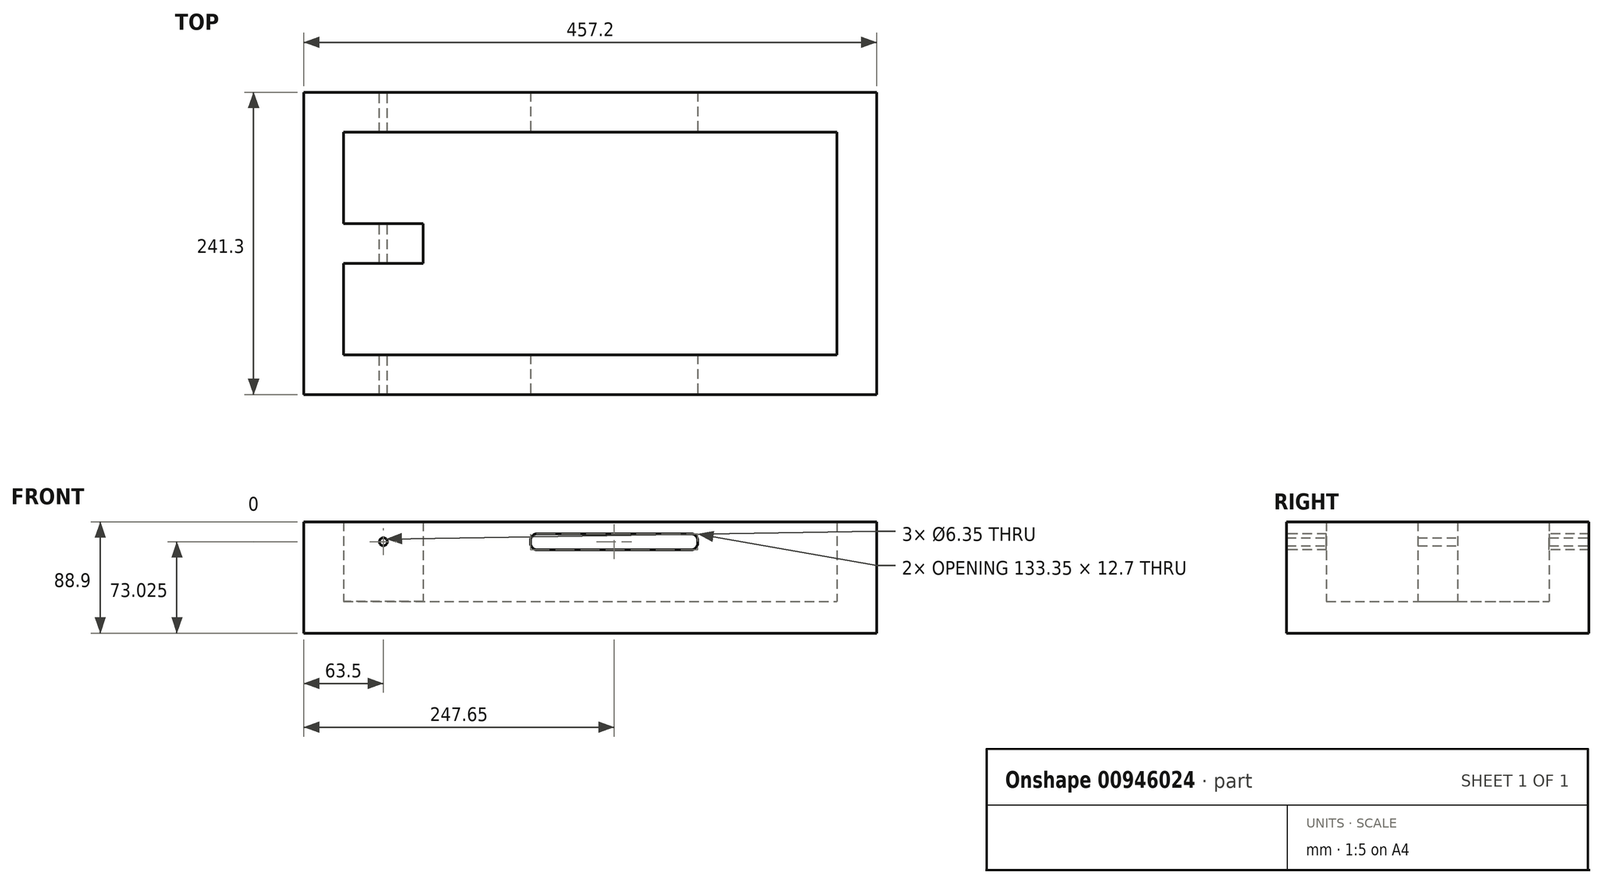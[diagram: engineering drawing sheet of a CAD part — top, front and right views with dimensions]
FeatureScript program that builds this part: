
annotation { "Feature Type Name" : "Feature", "Feature Type Description" : "" }
export const myFeature = defineFeature(function(context is Context, id is Id, definition is map)
    precondition{}
    {
        {
            var Q0;
            Q0=qCreatedBy(makeId("Front.planeOp"),FACE);
            var sketch = newSketch(context, id + "F0", { "sketchPlane" : qUnion([Q0])});
            skLineSegment(sketch, "E0.bottom", {"start": v(0, 0) * mm, "end": v(457.2, 0) * mm});
            skLineSegment(sketch, "E0.top", {"start": v(0, 63.5) * mm, "end": v(457.2, 63.5) * mm});
            skLineSegment(sketch, "E0.left", {"start": v(0, 0) * mm, "end": v(0, 63.5) * mm});
            skLineSegment(sketch, "E0.right", {"start": v(457.2, 0) * mm, "end": v(457.2, 63.5) * mm});
            skSolve(sketch);
        }
        {
            var Q0;
            Q0=makeQuery(id+"F0.imprint","IMPRINT",FACE,{"disambiguationData":[TD([[makeQuery(id+"F0.imprint","IMPRINT",EDGE,{"derivedFrom":sQuery(id+"F0.wireOp",EDGE,"E0.bottom")}),1.0]])]});
            extrude(context, id + "F1", {"entities" : qUnion([Q0]), "depth" : 31.75 * mm});
        }
        {
            var Q0;
            Q0=makeQuery(id+"F1.opExtrude","CAP_FACE",FACE,{"disambiguationData":[OSD([sQuery(id+"F0.wireOp",EDGE,"E0.bottom"),sQuery(id+"F0.wireOp",EDGE,"E0.top"),sQuery(id+"F0.wireOp",EDGE,"E0.left"),sQuery(id+"F0.wireOp",EDGE,"E0.right")])],"isStart":false});
            var sketch = newSketch(context, id + "F2", { "sketchPlane" : qUnion([Q0])});
            skLineSegment(sketch, "E1.bottom", {"start": v(457.2, 63.5) * mm, "end": v(425.45, 63.5) * mm});
            skLineSegment(sketch, "E1.top", {"start": v(457.2, 0) * mm, "end": v(425.45, 0) * mm});
            skLineSegment(sketch, "E1.left", {"start": v(457.2, 63.5) * mm, "end": v(457.2, 0) * mm});
            skLineSegment(sketch, "E1.right", {"start": v(425.45, 63.5) * mm, "end": v(425.45, 0) * mm});
            skSolve(sketch);
        }
        {
            var Q0;
            Q0=makeQuery(id+"F2.imprint","IMPRINT",FACE,{"disambiguationData":[TD([[makeQuery(id+"F2.imprint","IMPRINT",EDGE,{"derivedFrom":sQuery(id+"F2.wireOp",EDGE,"E1.bottom")}),-1.0]])]});
            extrude(context, id + "F3", {"entities" : qUnion([Q0]), "operationType" : NewBodyOperationType.ADD, "depth" : 177.8 * mm});
        }
        {
            var Q0;
            Q0=makeQuery(id+"F3.opExtrude","CAP_FACE",FACE,{"disambiguationData":[OSD([sQuery(id+"F2.wireOp",EDGE,"E1.bottom"),sQuery(id+"F2.wireOp",EDGE,"E1.top"),sQuery(id+"F2.wireOp",EDGE,"E1.left"),sQuery(id+"F2.wireOp",EDGE,"E1.right")])],"isStart":false});
            var sketch = newSketch(context, id + "F4", { "sketchPlane" : qUnion([Q0])});
            skLineSegment(sketch, "E2.bottom", {"start": v(457.2, 0) * mm, "end": v(0, 0) * mm});
            skLineSegment(sketch, "E2.top", {"start": v(457.2, 63.5) * mm, "end": v(0, 63.5) * mm});
            skLineSegment(sketch, "E2.left", {"start": v(457.2, 0) * mm, "end": v(457.2, 63.5) * mm});
            skLineSegment(sketch, "E2.right", {"start": v(0, 0) * mm, "end": v(0, 63.5) * mm});
            skSolve(sketch);
        }
        {
            var Q0;
            {var subQ0=sQuery(id+"F4.wireOp",EDGE,"E2.left");Q0=makeQuery(id+"F4.imprint","IMPRINT",FACE,{"disambiguationData":[TD([[makeQuery(id+"F4.imprint","IMPRINT",EDGE,{"derivedFrom":subQ0}),1.0]])]});}
            var Q1;
            {var subQ2=sQuery(id+"F4.wireOp",EDGE,"E2.right");Q1=makeQuery(id+"F4.imprint","IMPRINT",FACE,{"disambiguationData":[TD([[makeQuery(id+"F4.imprint","IMPRINT",EDGE,{"derivedFrom":subQ2}),-1.0]])]});}
            extrude(context, id + "F5", {"entities" : qUnion([Q0, Q1]), "operationType" : NewBodyOperationType.ADD, "depth" : 31.75 * mm});
        }
        {
            var Q0;
            Q0=makeQuery(id+"F1.opExtrude","CAP_FACE",FACE,{"disambiguationData":[OSD([sQuery(id+"F0.wireOp",EDGE,"E0.bottom"),sQuery(id+"F0.wireOp",EDGE,"E0.top"),sQuery(id+"F0.wireOp",EDGE,"E0.left"),sQuery(id+"F0.wireOp",EDGE,"E0.right")])],"isStart":false});
            var sketch = newSketch(context, id + "F6", { "sketchPlane" : qUnion([Q0])});
            skLineSegment(sketch, "E3.bottom", {"start": v(0, 63.5) * mm, "end": v(31.75, 63.5) * mm});
            skLineSegment(sketch, "E3.top", {"start": v(0, 0) * mm, "end": v(31.75, 0) * mm});
            skLineSegment(sketch, "E3.left", {"start": v(0, 63.5) * mm, "end": v(0, 0) * mm});
            skLineSegment(sketch, "E3.right", {"start": v(31.75, 63.5) * mm, "end": v(31.75, 0) * mm});
            skSolve(sketch);
        }
        {
            var Q0;
            Q0=makeQuery(id+"F6.imprint","IMPRINT",FACE,{"disambiguationData":[TD([[makeQuery(id+"F6.imprint","IMPRINT",EDGE,{"derivedFrom":sQuery(id+"F6.wireOp",EDGE,"E3.bottom")}),-1.0]])]});
            extrude(context, id + "F7", {"entities" : qUnion([Q0]), "operationType" : NewBodyOperationType.ADD, "depth" : 177.8 * mm});
        }
        {
            var Q0;
            Q0=makeQuery(id+"F7.opExtrude","SWEPT_FACE",FACE,{"disambiguationData":[OSD([sQuery(id+"F6.wireOp",EDGE,"E3.right")])]});
            var sketch = newSketch(context, id + "F8", { "sketchPlane" : qUnion([Q0])});
            skLineSegment(sketch, "E4", {"start": v(-209.55, 63.5) * mm, "end": v(-120.65, 63.5) * mm});
            skLineSegment(sketch, "E5", {"start": v(-120.65, 63.5) * mm, "end": v(-120.65, 0) * mm});
            skLineSegment(sketch, "E6.bottom", {"start": v(-136.53, 63.5) * mm, "end": v(-104.78, 63.5) * mm});
            skLineSegment(sketch, "E6.top", {"start": v(-136.53, 0) * mm, "end": v(-104.78, 0) * mm});
            skLineSegment(sketch, "E6.left", {"start": v(-136.53, 63.5) * mm, "end": v(-136.53, 0) * mm});
            skLineSegment(sketch, "E6.right", {"start": v(-104.78, 63.5) * mm, "end": v(-104.78, 0) * mm});
            skPoint(sketch, "E6.middle", {"position": v(-120.65, 31.75) * mm});
            skSolve(sketch);
        }
        {
            var Q0;
            {var subQ0=sQuery(id+"F8.wireOp",EDGE,"E5");Q0=makeQuery(id+"F8.imprint","IMPRINT",FACE,{"disambiguationData":[TD([[makeQuery(id+"F8.imprint","IMPRINT",EDGE,{"derivedFrom":subQ0}),-1.0]])]});}
            var Q1;
            {var subQ0=sQuery(id+"F8.wireOp",EDGE,"E5");Q1=makeQuery(id+"F8.imprint","IMPRINT",FACE,{"disambiguationData":[TD([[makeQuery(id+"F8.imprint","IMPRINT",EDGE,{"derivedFrom":subQ0}),1.0]])]});}
            extrude(context, id + "F9", {"entities" : qUnion([Q0, Q1]), "operationType" : NewBodyOperationType.ADD, "depth" : 63.5 * mm});
        }
        {
            var Q0;
            Q0=makeQuery(id+"F9.opExtrude","SWEPT_FACE",FACE,{"disambiguationData":[OSD([sQuery(id+"F8.wireOp",EDGE,"E6.left")])]});
            var sketch = newSketch(context, id + "F10", { "sketchPlane" : qUnion([Q0])});
            skCircle(sketch, "E7", {"center": v(63.5, 47.62) * mm, "radius": 3.18 * mm});
            skPoint(sketch, "E7.centerSnap0", {"position": v(31.75, 31.75) * mm});
            skPoint(sketch, "E7.centerSnap1", {"position": v(63.5, 63.5) * mm});
            skSolve(sketch);
        }
        {
            var Q0;
            Q0=qSketchRegion(id+"F10",true);
            extrude(context, id + "F11", {"entities" : qUnion([Q0]), "operationType" : NewBodyOperationType.REMOVE, "endBound" : BoundingType.SYMMETRIC, "depth" : 381 * mm});
        }
        {
            var Q0;
            Q0=makeQuery(id+"F9.boolean.opBoolean","MERGE",FACE,{"derivedFrom":[makeQuery(id+"F7.boolean.opBoolean","MERGE",FACE,{"derivedFrom":[makeQuery(id+"F5.boolean.opBoolean","MERGE",FACE,{"derivedFrom":[makeQuery(id+"F3.boolean.opBoolean","MERGE",FACE,{"derivedFrom":[makeQuery(id+"F1.opExtrude","SWEPT_FACE",FACE,{"disambiguationData":[OSD([sQuery(id+"F0.wireOp",EDGE,"E0.bottom")])]}),makeQuery(id+"F3.opExtrude","SWEPT_FACE",FACE,{"disambiguationData":[OSD([sQuery(id+"F2.wireOp",EDGE,"E1.top")])]})]}),makeQuery(id+"F5.opExtrude","SWEPT_FACE",FACE,{"disambiguationData":[OSD([sQuery(id+"F4.wireOp",EDGE,"E2.bottom")])]})]}),makeQuery(id+"F7.opExtrude","SWEPT_FACE",FACE,{"disambiguationData":[OSD([sQuery(id+"F6.wireOp",EDGE,"E3.top")])]})]}),makeQuery(id+"F9.opExtrude","SWEPT_FACE",FACE,{"disambiguationData":[OSD([sQuery(id+"F8.wireOp",EDGE,"E6.top")])]})]});
            var sketch = newSketch(context, id + "F12", { "sketchPlane" : qUnion([Q0])});
            skLineSegment(sketch, "E8.bottom", {"start": v(0, 241.3) * mm, "end": v(457.2, 241.3) * mm});
            skLineSegment(sketch, "E8.top", {"start": v(0, 0) * mm, "end": v(457.2, 0) * mm});
            skLineSegment(sketch, "E8.left", {"start": v(0, 241.3) * mm, "end": v(0, 0) * mm});
            skLineSegment(sketch, "E8.right", {"start": v(457.2, 241.3) * mm, "end": v(457.2, 0) * mm});
            skSolve(sketch);
        }
        {
            var Q0;
            Q0=makeQuery(id+"F12.imprint","IMPRINT",FACE,{"disambiguationData":[TD([[makeQuery(id+"F12.imprint","IMPRINT",EDGE,{"derivedFrom":sQuery(id+"F12.wireOp",EDGE,"E8.bottom")}),-1.0]])]});
            var Q1;
            {var subQ4=sQuery(id+"F0.wireOp",EDGE,"E0.bottom");Q1=makeQuery(id+"F12.imprint","IMPRINT",FACE,{"disambiguationData":[TD([[makeQuery(id+"F12.imprint","IMPRINT",EDGE,{"derivedFrom":makeQuery(id+"F1.opExtrude","CAP_EDGE",EDGE,{"disambiguationData":[OSD([subQ4])],"isStart":false})}),1.0]])]});}
            extrude(context, id + "F13", {"entities" : qUnion([Q0, Q1]), "operationType" : NewBodyOperationType.ADD, "depth" : 25.4 * mm});
        }
        {
            var Q0;
            Q0=makeQuery(id+"F13.boolean.opBoolean","MERGE",FACE,{"derivedFrom":[makeQuery(id+"F5.opExtrude","CAP_FACE",FACE,{"disambiguationData":[OSD([sQuery(id+"F4.wireOp",EDGE,"E2.bottom"),sQuery(id+"F4.wireOp",EDGE,"E2.top"),sQuery(id+"F4.wireOp",EDGE,"E2.left"),sQuery(id+"F4.wireOp",EDGE,"E2.right")])],"isStart":false}),makeQuery(id+"F13.opExtrude","SWEPT_FACE",FACE,{"disambiguationData":[OSD([sQuery(id+"F12.wireOp",EDGE,"E8.bottom")])]})]});
            var sketch = newSketch(context, id + "F14", { "sketchPlane" : qUnion([Q0])});
            skLineSegment(sketch, "E9", {"start": v(457.2, 63.5) * mm, "end": v(393.7, 63.5) * mm});
            skLineSegment(sketch, "E10", {"start": v(393.7, 63.5) * mm, "end": v(101.6, 63.5) * mm});
            skLineSegment(sketch, "E11", {"start": v(101.6, 63.5) * mm, "end": v(247.65, 63.5) * mm});
            skLineSegment(sketch, "E12", {"start": v(247.65, 63.5) * mm, "end": v(247.65, 47.62) * mm});
            skLineSegment(sketch, "E13.bottom", {"start": v(314.33, 41.28) * mm, "end": v(180.98, 41.28) * mm});
            skLineSegment(sketch, "E13.top", {"start": v(314.33, 53.97) * mm, "end": v(180.98, 53.97) * mm});
            skLineSegment(sketch, "E13.left", {"start": v(314.33, 41.28) * mm, "end": v(314.33, 53.98) * mm});
            skLineSegment(sketch, "E13.right", {"start": v(180.98, 41.28) * mm, "end": v(180.98, 53.98) * mm});
            skPoint(sketch, "E13.middle", {"position": v(247.65, 47.62) * mm});
            skSolve(sketch);
        }
        {
            var Q0;
            Q0=makeQuery(id+"F14.imprint","IMPRINT",FACE,{"disambiguationData":[TD([[makeQuery(id+"F14.imprint","IMPRINT",EDGE,{"derivedFrom":sQuery(id+"F14.wireOp",EDGE,"E13.bottom")}),-1.0]])]});
            extrude(context, id + "F15", {"entities" : qUnion([Q0]), "operationType" : NewBodyOperationType.REMOVE, "oppositeDirection" : true, "depth" : 254 * mm});
        }
        {
            var Q0;
            {var subQ4=sQuery(id+"F14.wireOp",EDGE,"E13.bottom");var subQ5=sQuery(id+"F14.wireOp",EDGE,"E13.right");Q0=makeQuery(id+"F15.boolean.opBoolean","COPY",EDGE,{"disambiguationData":[TD([makeQuery(id+"F13.opExtrude","SWEPT_FACE",FACE,{"disambiguationData":[OSD([sQuery(id+"F12.wireOp",EDGE,"E8.bottom")])]})])],"derivedFrom":makeQuery(id+"F15.opExtrude","SWEPT_EDGE",EDGE,{"disambiguationData":[OSD([subQ4,subQ5])]})});}
            var Q1;
            {var subQ4=sQuery(id+"F14.wireOp",EDGE,"E13.top");var subQ5=sQuery(id+"F14.wireOp",EDGE,"E13.right");Q1=makeQuery(id+"F15.boolean.opBoolean","COPY",EDGE,{"disambiguationData":[TD([makeQuery(id+"F13.opExtrude","SWEPT_FACE",FACE,{"disambiguationData":[OSD([sQuery(id+"F12.wireOp",EDGE,"E8.bottom")])]})])],"derivedFrom":makeQuery(id+"F15.opExtrude","SWEPT_EDGE",EDGE,{"disambiguationData":[OSD([subQ4,subQ5])]})});}
            var Q2;
            {var subQ4=sQuery(id+"F14.wireOp",EDGE,"E13.bottom");var subQ5=sQuery(id+"F14.wireOp",EDGE,"E13.left");Q2=makeQuery(id+"F15.boolean.opBoolean","COPY",EDGE,{"disambiguationData":[TD([makeQuery(id+"F13.opExtrude","SWEPT_FACE",FACE,{"disambiguationData":[OSD([sQuery(id+"F12.wireOp",EDGE,"E8.bottom")])]})])],"derivedFrom":makeQuery(id+"F15.opExtrude","SWEPT_EDGE",EDGE,{"disambiguationData":[OSD([subQ4,subQ5])]})});}
            var Q3;
            {var subQ4=sQuery(id+"F14.wireOp",EDGE,"E13.top");var subQ5=sQuery(id+"F14.wireOp",EDGE,"E13.left");Q3=makeQuery(id+"F15.boolean.opBoolean","COPY",EDGE,{"disambiguationData":[TD([makeQuery(id+"F13.opExtrude","SWEPT_FACE",FACE,{"disambiguationData":[OSD([sQuery(id+"F12.wireOp",EDGE,"E8.bottom")])]})])],"derivedFrom":makeQuery(id+"F15.opExtrude","SWEPT_EDGE",EDGE,{"disambiguationData":[OSD([subQ4,subQ5])]})});}
            var Q4;
            {var subQ0=sQuery(id+"F14.wireOp",EDGE,"E13.bottom");var subQ5=sQuery(id+"F14.wireOp",EDGE,"E13.right");Q4=makeQuery(id+"F15.boolean.opBoolean","COPY",EDGE,{"disambiguationData":[TD([makeQuery(id+"F13.opExtrude","SWEPT_FACE",FACE,{"disambiguationData":[OSD([sQuery(id+"F12.wireOp",EDGE,"E8.top")])]})])],"derivedFrom":makeQuery(id+"F15.opExtrude","SWEPT_EDGE",EDGE,{"disambiguationData":[OSD([subQ0,subQ5])]})});}
            var Q5;
            {var subQ0=sQuery(id+"F14.wireOp",EDGE,"E13.top");var subQ5=sQuery(id+"F14.wireOp",EDGE,"E13.right");Q5=makeQuery(id+"F15.boolean.opBoolean","COPY",EDGE,{"disambiguationData":[TD([makeQuery(id+"F13.opExtrude","SWEPT_FACE",FACE,{"disambiguationData":[OSD([sQuery(id+"F12.wireOp",EDGE,"E8.top")])]})])],"derivedFrom":makeQuery(id+"F15.opExtrude","SWEPT_EDGE",EDGE,{"disambiguationData":[OSD([subQ0,subQ5])]})});}
            var Q6;
            {var subQ0=sQuery(id+"F14.wireOp",EDGE,"E13.bottom");var subQ5=sQuery(id+"F14.wireOp",EDGE,"E13.left");Q6=makeQuery(id+"F15.boolean.opBoolean","COPY",EDGE,{"disambiguationData":[TD([makeQuery(id+"F13.opExtrude","SWEPT_FACE",FACE,{"disambiguationData":[OSD([sQuery(id+"F12.wireOp",EDGE,"E8.top")])]})])],"derivedFrom":makeQuery(id+"F15.opExtrude","SWEPT_EDGE",EDGE,{"disambiguationData":[OSD([subQ0,subQ5])]})});}
            var Q7;
            {var subQ0=sQuery(id+"F14.wireOp",EDGE,"E13.top");var subQ5=sQuery(id+"F14.wireOp",EDGE,"E13.left");Q7=makeQuery(id+"F15.boolean.opBoolean","COPY",EDGE,{"disambiguationData":[TD([makeQuery(id+"F13.opExtrude","SWEPT_FACE",FACE,{"disambiguationData":[OSD([sQuery(id+"F12.wireOp",EDGE,"E8.top")])]})])],"derivedFrom":makeQuery(id+"F15.opExtrude","SWEPT_EDGE",EDGE,{"disambiguationData":[OSD([subQ0,subQ5])]})});}
            fillet(context, id + "F16", {"entities" : qUnion([Q0, Q1, Q2, Q3, Q4, Q5, Q6, Q7]), "radius" : 5.08 * mm, "tangentPropagation" : true, "allowEdgeOverflow" : false});
        }
    });
